# Revit family: T400009
name_source: partatom
category: Furniture
revit_build: Autodesk Revit Architecture 2013 (Build: 20120221_2030(x64)
units: mm (PartAtom-declared; Revit-internal decimal feet)

## types (1)
- T400009
    Assembly Code = E2020200
    Back Coverage Material = OFS BRANDS INTERMIX Back Coverage Plastic
    Catalog = http://ofsbrands.com
    Chassis Material = OFS BRANDS INTERMIX Chassis Wood
    Conector Clip Material = OFS BRANDS INTERMIX Conector Clip Metal
    Depth = 107 1/16"
    Description = OFS BRANDS FIRST OFFICE INTERMIX TYPICAL T400009
    Door Material = OFS BRANDS INTERMIX Door Plastic
    Feet Material = OFS BRANDS INTERMIX Feet Metal
    Height = 72"
    Manufacturer = FIRST OFFICE
    Model = T400009
    Pull Material = OFS BRANDS INTERMIX Pull Metal
    Top Core Material = OFS BRANDS INTERMIX Top Core Wood
    URL = http://www.ofsbrands.com
    Width = 168 5/16"

## geometry (parser evidence)
native form markers: Blend x12, Sweep x1
no freeform markers — native parametric forms only
